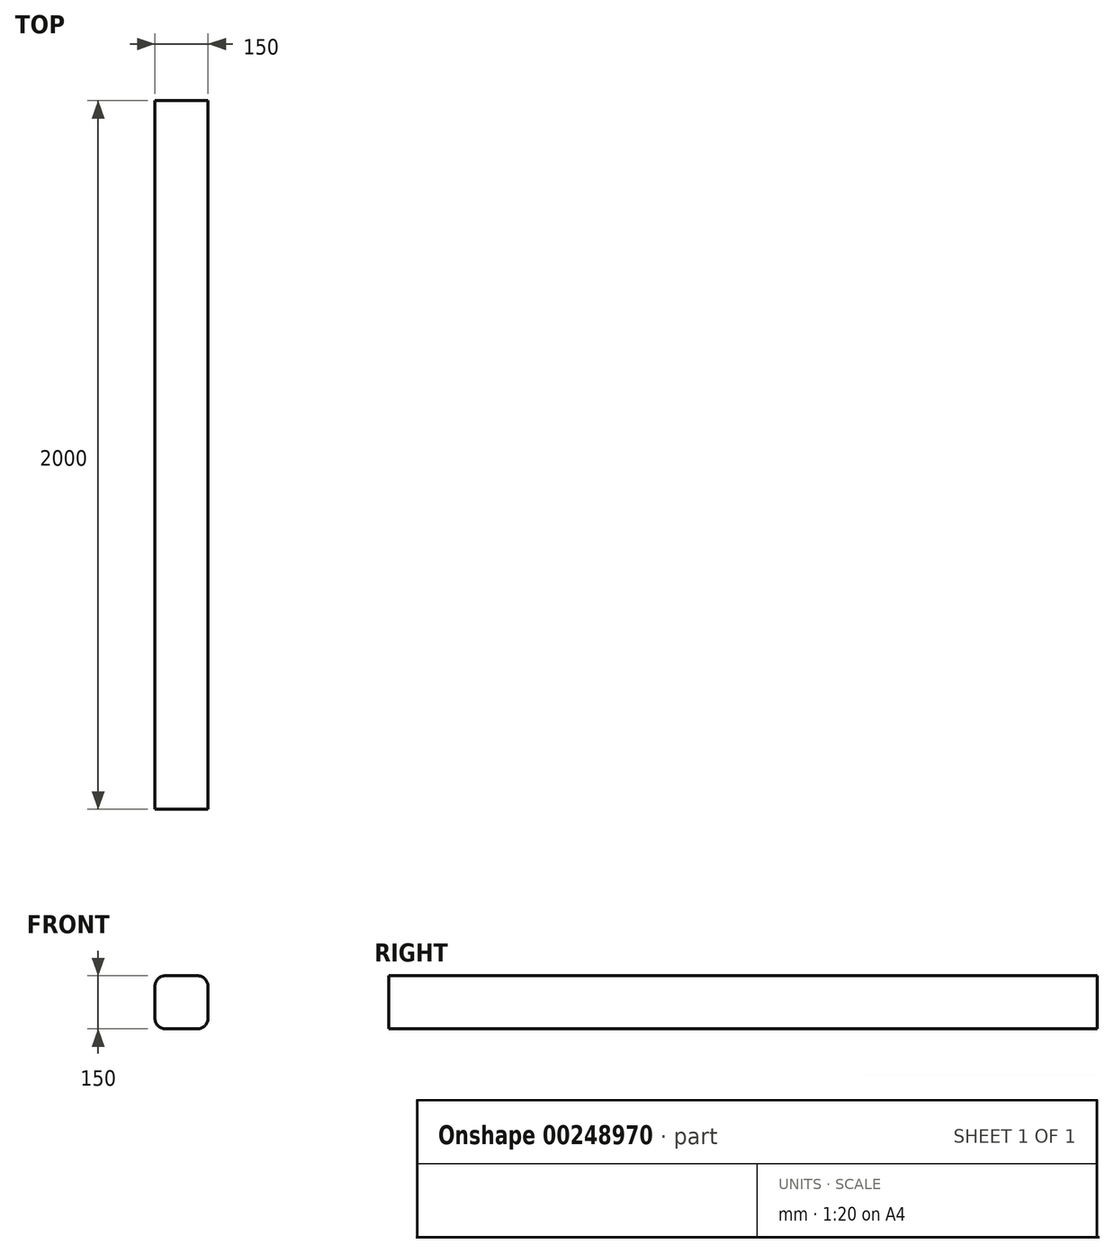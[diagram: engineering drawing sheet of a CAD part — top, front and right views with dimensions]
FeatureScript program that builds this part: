
annotation { "Feature Type Name" : "Feature", "Feature Type Description" : "" }
export const myFeature = defineFeature(function(context is Context, id is Id, definition is map)
    precondition{}
    {
        {
            var Q0;
            Q0=qCreatedBy(makeId("Front.planeOp"),FACE);
            var sketch = newSketch(context, id + "F0", { "sketchPlane" : qUnion([Q0])});
            skLineSegment(sketch, "E0.bottom", {"start": v(45, 75) * mm, "end": v(-45, 75) * mm});
            skLineSegment(sketch, "E0.top", {"start": v(45, -75) * mm, "end": v(-45, -75) * mm});
            skLineSegment(sketch, "E0.left", {"start": v(75, 45) * mm, "end": v(75, -45) * mm});
            skLineSegment(sketch, "E0.right", {"start": v(-75, 45) * mm, "end": v(-75, -45) * mm});
            skPoint(sketch, "E0.middle", {"position": v(0, 0) * mm});
            skPoint(sketch, "E1.visualSharp", {"position": v(75, 75) * mm});
            skArc(sketch, "E1.filletArc", {"start": v(75, 45) * mm, "mid": v(66.21, 66.21) * mm, "end": v(45, 75) * mm});
            skPoint(sketch, "E2.visualSharp", {"position": v(75, -75) * mm});
            skArc(sketch, "E2.filletArc", {"start": v(45, -75) * mm, "mid": v(66.21, -66.21) * mm, "end": v(75, -45) * mm});
            skPoint(sketch, "E3.visualSharp", {"position": v(-75, -75) * mm});
            skArc(sketch, "E3.filletArc", {"start": v(-75, -45) * mm, "mid": v(-66.21, -66.21) * mm, "end": v(-45, -75) * mm});
            skPoint(sketch, "E4.visualSharp", {"position": v(-75, 75) * mm});
            skArc(sketch, "E4.filletArc", {"start": v(-45, 75) * mm, "mid": v(-66.21, 66.21) * mm, "end": v(-75, 45) * mm});
            skSolve(sketch);
        }
        {
            var Q0;
            Q0 = qSketchRegion(id + "F0", true);
            extrude(context, id + "F1", {"entities" : qUnion([Q0]), "depth" : 2000 * mm});
        }
    });
